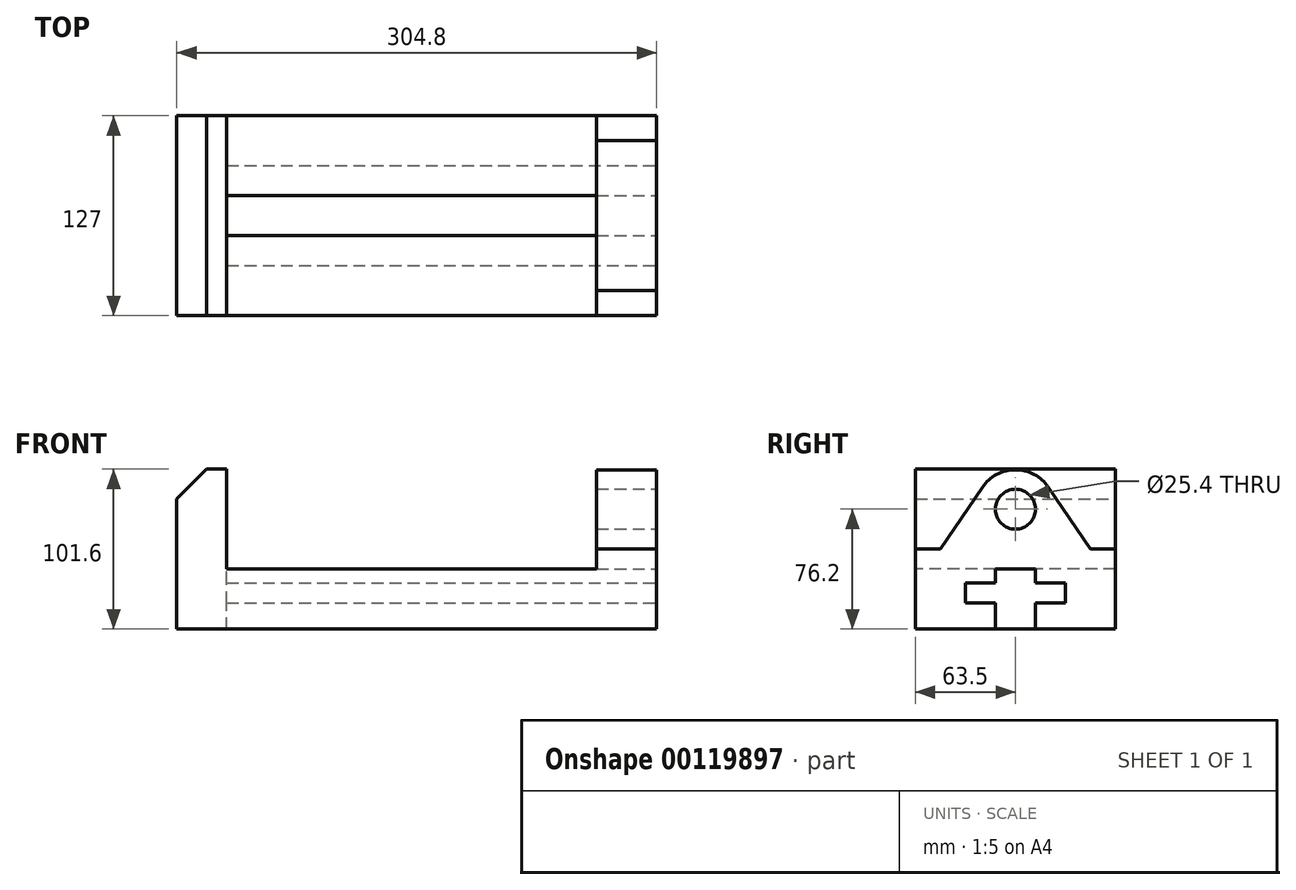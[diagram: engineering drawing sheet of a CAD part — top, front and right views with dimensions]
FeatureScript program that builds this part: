
annotation { "Feature Type Name" : "Feature", "Feature Type Description" : "" }
export const myFeature = defineFeature(function(context is Context, id is Id, definition is map)
    precondition{}
    {
        {
            var Q0;
            Q0=qCreatedBy(makeId("Front.planeOp"),FACE);
            var sketch = newSketch(context, id + "F0", { "sketchPlane" : qUnion([Q0])});
            skLineSegment(sketch, "E0", {"start": v(0, 0) * mm, "end": v(0, 101.6) * mm});
            skLineSegment(sketch, "E1", {"start": v(0, 101.6) * mm, "end": v(31.75, 101.6) * mm});
            skLineSegment(sketch, "E2", {"start": v(31.75, 101.6) * mm, "end": v(31.75, 38.1) * mm});
            skLineSegment(sketch, "E3", {"start": v(31.75, 38.1) * mm, "end": v(266.7, 38.1) * mm});
            skLineSegment(sketch, "E4", {"start": v(266.7, 38.1) * mm, "end": v(266.7, 101.6) * mm});
            skLineSegment(sketch, "E5", {"start": v(266.7, 101.6) * mm, "end": v(304.8, 101.6) * mm});
            skLineSegment(sketch, "E6", {"start": v(304.8, 101.6) * mm, "end": v(304.8, 0) * mm});
            skLineSegment(sketch, "E7", {"start": v(304.8, 0) * mm, "end": v(0, 0) * mm});
            skLineSegment(sketch, "E8", {"start": v(266.7, 50.8) * mm, "end": v(304.8, 50.8) * mm});
            skSolve(sketch);
        }
        {
            var Q0;
            Q0=makeQuery(id+"F0.imprint","IMPRINT",FACE,{"disambiguationData":[TD([[makeQuery(id+"F0.imprint","IMPRINT",EDGE,{"derivedFrom":sQuery(id+"F0.wireOp",EDGE,"E0")}),-1.0]])]});
            var Q1;
            {var subQ0=sQuery(id+"F0.wireOp",EDGE,"E5");Q1=makeQuery(id+"F0.imprint","IMPRINT",FACE,{"disambiguationData":[TD([[makeQuery(id+"F0.imprint","IMPRINT",EDGE,{"derivedFrom":subQ0}),-1.0]])]});}
            extrude(context, id + "F1", {"entities" : qUnion([Q0, Q1]), "oppositeDirection" : true, "depth" : 127 * mm});
        }
        {
            var Q0;
            Q0=makeQuery(id+"F1.opExtrude","SWEPT_EDGE",EDGE,{"disambiguationData":[OSD([sQuery(id+"F0.wireOp",EDGE,"E0"),sQuery(id+"F0.wireOp",EDGE,"E1")])]});
            chamfer(context, id + "F2", {"entities" : qUnion([Q0]), "chamferType" : ChamferType.TWO_OFFSETS, "width1" : 19.05 * mm, "oppositeDirection" : false, "width2" : 19.05 * mm, "tangentPropagation" : true});
        }
        {
            var Q0;
            Q0=makeQuery(id+"F1.opExtrude","SWEPT_FACE",FACE,{"disambiguationData":[OSD([sQuery(id+"F0.wireOp",EDGE,"E6")])]});
            var sketch = newSketch(context, id + "F3", { "sketchPlane" : qUnion([Q0])});
            skLineSegment(sketch, "E9", {"start": v(63.5, 177.8) * mm, "end": v(63.5, 0) * mm, "construction": true});
            skLineSegment(sketch, "E10", {"start": v(0, 50.8) * mm, "end": v(15.88, 50.8) * mm});
            skLineSegment(sketch, "E11", {"start": v(50.8, 0) * mm, "end": v(50.8, 16.5) * mm});
            skLineSegment(sketch, "E12", {"start": v(50.8, 16.5) * mm, "end": v(31.75, 16.5) * mm});
            skLineSegment(sketch, "E13", {"start": v(31.75, 16.5) * mm, "end": v(31.75, 29.2) * mm});
            skLineSegment(sketch, "E14", {"start": v(31.75, 29.2) * mm, "end": v(50.8, 29.2) * mm});
            skLineSegment(sketch, "E15", {"start": v(50.8, 29.2) * mm, "end": v(50.8, 38.1) * mm});
            skLineSegment(sketch, "E16", {"start": v(50.8, 38.1) * mm, "end": v(63.5, 38.1) * mm});
            skLineSegment(sketch, "E17", {"start": v(50.8, 0) * mm, "end": v(63.5, 0) * mm});
            skLineSegment(sketch, "E18.MirrorCS", {"start": v(127, 50.8) * mm, "end": v(111.12, 50.8) * mm});
            skLineSegment(sketch, "E19.MirrorCS", {"start": v(76.2, 38.1) * mm, "end": v(63.5, 38.1) * mm});
            skLineSegment(sketch, "E20.MirrorCS", {"start": v(76.2, 29.2) * mm, "end": v(76.2, 38.1) * mm});
            skLineSegment(sketch, "E21.MirrorCS", {"start": v(95.25, 29.2) * mm, "end": v(76.2, 29.2) * mm});
            skLineSegment(sketch, "E22.MirrorCS", {"start": v(95.25, 16.5) * mm, "end": v(95.25, 29.2) * mm});
            skLineSegment(sketch, "E23.MirrorCS", {"start": v(76.2, 16.5) * mm, "end": v(95.25, 16.5) * mm});
            skLineSegment(sketch, "E24.MirrorCS", {"start": v(76.2, 0) * mm, "end": v(76.2, 16.5) * mm});
            skCircle(sketch, "E25", {"center": v(63.5, 76.2) * mm, "radius": 12.7 * mm});
            skArc(sketch, "E26", {"start": v(84.54, 90.1) * mm, "mid": v(63.5, 101.26) * mm, "end": v(42.46, 90.1) * mm});
            skLineSegment(sketch, "E27", {"start": v(15.88, 50.8) * mm, "end": v(42.46, 90.1) * mm});
            skLineSegment(sketch, "E28", {"start": v(84.54, 90.1) * mm, "end": v(111.12, 50.8) * mm});
            skSolve(sketch);
        }
        {
            var Q0;
            Q0=makeQuery(id+"F3.imprint","IMPRINT",FACE,{"disambiguationData":[TD([[makeQuery(id+"F3.imprint","IMPRINT",EDGE,{"derivedFrom":sQuery(id+"F3.wireOp",EDGE,"E11")}),-1.0]])]});
            var Q1;
            Q1=makeQuery(id+"F1.opExtrude","SWEPT_FACE",FACE,{"disambiguationData":[OSD([sQuery(id+"F0.wireOp",EDGE,"E2")])]});
            extrude(context, id + "F4", {"entities" : qUnion([Q0]), "operationType" : NewBodyOperationType.REMOVE, "endBound" : BoundingType.UP_TO_SURFACE, "oppositeDirection" : true, "endBoundEntityFace" : qUnion([Q1]), "depth" : 25.4 * mm});
        }
        {
            var Q0;
            Q0=makeQuery(id+"F3.imprint","IMPRINT",FACE,{"disambiguationData":[TD([[makeQuery(id+"F3.imprint","IMPRINT",EDGE,{"derivedFrom":sQuery(id+"F3.wireOp",EDGE,"E25")}),1.0]])]});
            extrude(context, id + "F5", {"entities" : qUnion([Q0]), "operationType" : NewBodyOperationType.REMOVE, "oppositeDirection" : true, "depth" : 38.1 * mm});
        }
        {
            var Q0;
            {var subQ3=sQuery(id+"F3.wireOp",EDGE,"E10");Q0=makeQuery(id+"F3.imprint","IMPRINT",FACE,{"disambiguationData":[TD([[makeQuery(id+"F3.imprint","IMPRINT",EDGE,{"derivedFrom":subQ3}),1.0]])]});}
            extrude(context, id + "F6", {"entities" : qUnion([Q0]), "operationType" : NewBodyOperationType.REMOVE, "oppositeDirection" : true, "depth" : 38.1 * mm});
        }
    });
